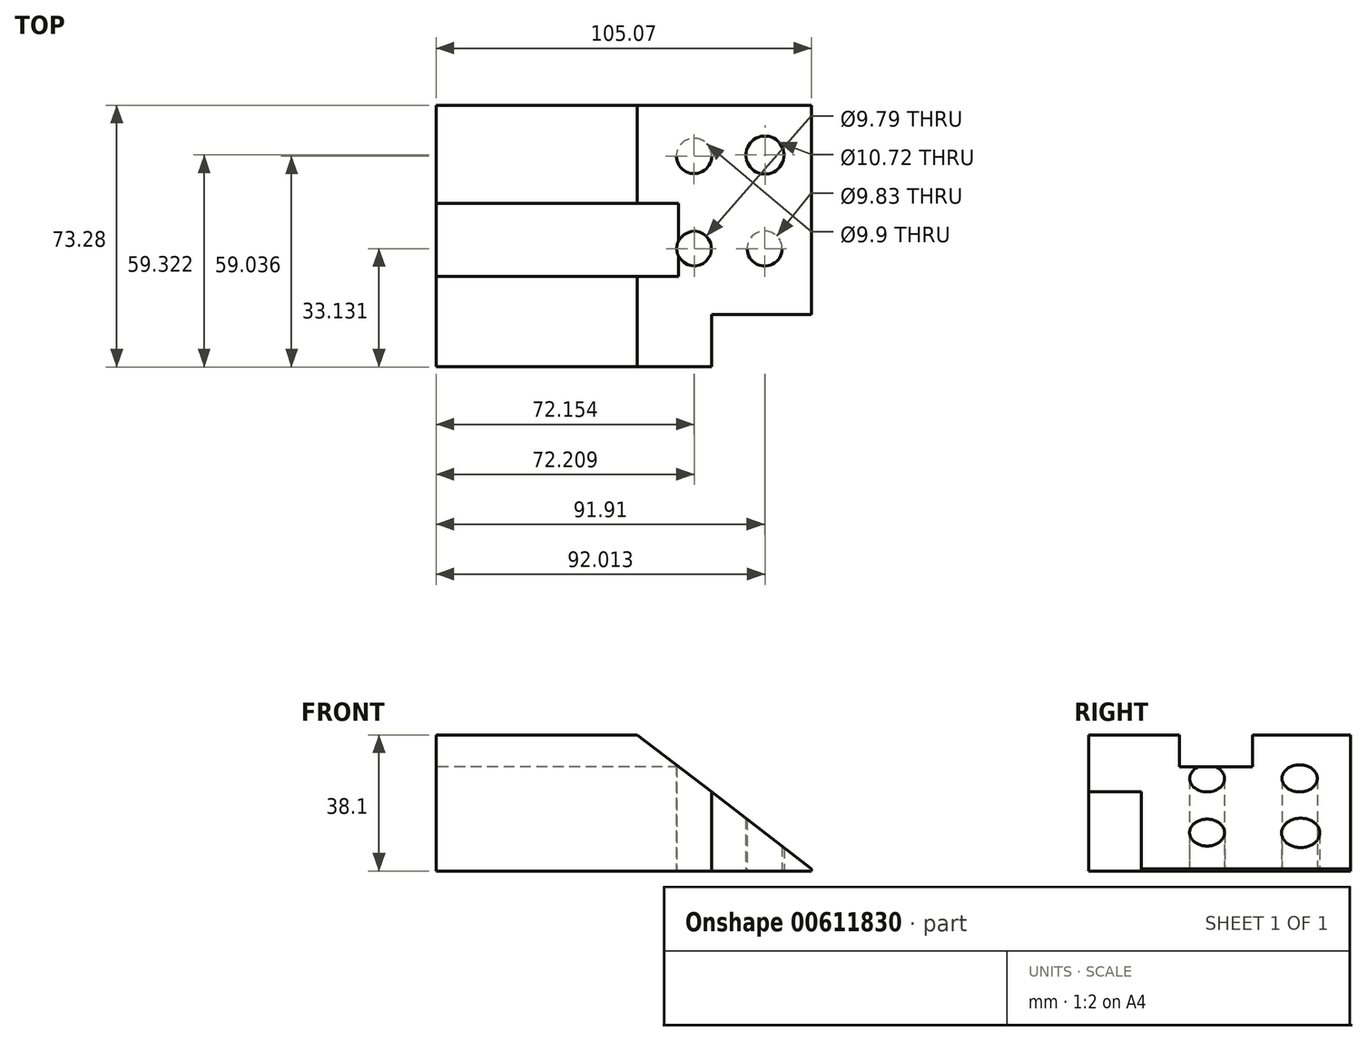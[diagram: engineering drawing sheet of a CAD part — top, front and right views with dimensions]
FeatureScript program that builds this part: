
annotation { "Feature Type Name" : "Feature", "Feature Type Description" : "" }
export const myFeature = defineFeature(function(context is Context, id is Id, definition is map)
    precondition{}
    {
        {
            var Q0;
            Q0=qCreatedBy(makeId("Top.planeOp"),FACE);
            var sketch = newSketch(context, id + "F0", { "sketchPlane" : qUnion([Q0])});
            skLineSegment(sketch, "E0.bottom", {"start": v(0, 0) * mm, "end": v(-59.7, 0) * mm});
            skLineSegment(sketch, "E0.top", {"start": v(0, -73.28) * mm, "end": v(-59.7, -73.28) * mm});
            skLineSegment(sketch, "E0.left", {"start": v(0, 0) * mm, "end": v(0, -73.28) * mm});
            skLineSegment(sketch, "E0.right", {"start": v(-59.7, 0) * mm, "end": v(-59.7, -73.28) * mm});
            skLineSegment(sketch, "E1.bottom", {"start": v(0, 0) * mm, "end": v(45.38, 0) * mm});
            skLineSegment(sketch, "E1.top", {"start": v(0, -73.28) * mm, "end": v(45.38, -73.28) * mm});
            skLineSegment(sketch, "E1.right", {"start": v(45.38, 0) * mm, "end": v(45.38, -73.28) * mm});
            skSolve(sketch);
        }
        {
            var Q0;
            Q0 = qSketchRegion(id + "F0", true);
            extrude(context, id + "F1", {"entities" : qUnion([Q0]), "depth" : 38.1 * mm, "offsetDistance" : 25.4 * mm});
        }
        {
            var Q0;
            Q0=qCreatedBy(makeId("Front.planeOp"),FACE);
            var sketch = newSketch(context, id + "F2", { "sketchPlane" : qUnion([Q0])});
            skLineSegment(sketch, "E2", {"start": v(46.2, 0) * mm, "end": v(-9.07, 42.45) * mm});
            skLineSegment(sketch, "E3", {"start": v(-9.07, 42.45) * mm, "end": v(48.2, 42.45) * mm});
            skLineSegment(sketch, "E4", {"start": v(48.2, 42.45) * mm, "end": v(48.2, 0) * mm});
            skLineSegment(sketch, "E5", {"start": v(48.2, 0) * mm, "end": v(46.2, 0) * mm});
            skSolve(sketch);
        }
        {
            var Q0;
            Q0=makeQuery(id+"F2.imprint","IMPRINT",FACE,{"disambiguationData":[TD([[makeQuery(id+"F2.imprint","IMPRINT",EDGE,{"derivedFrom":sQuery(id+"F2.wireOp",EDGE,"E2")}),-1.0]])]});
            extrude(context, id + "F3", {"entities" : qUnion([Q0]), "operationType" : NewBodyOperationType.REMOVE, "oppositeDirection" : true, "depth" : -76.2 * mm, "offsetDistance" : 25.4 * mm});
        }
        {
            var Q0;
            Q0=makeQuery(id+"F1.opExtrude","SWEPT_FACE",FACE,{"disambiguationData":[OSD([sQuery(id+"F0.wireOp",EDGE,"E0.right")])]});
            var sketch = newSketch(context, id + "F4", { "sketchPlane" : qUnion([Q0])});
            skLineSegment(sketch, "E6", {"start": v(27.49, 38.1) * mm, "end": v(27.49, 29.21) * mm});
            skLineSegment(sketch, "E7", {"start": v(27.49, 29.21) * mm, "end": v(47.92, 29.21) * mm});
            skLineSegment(sketch, "E8", {"start": v(47.92, 29.21) * mm, "end": v(47.92, 38.1) * mm});
            skLineSegment(sketch, "E9", {"start": v(47.92, 38.1) * mm, "end": v(27.49, 38.1) * mm});
            skSolve(sketch);
        }
        {
            var Q0;
            Q0 = qSketchRegion(id + "F4", true);
            extrude(context, id + "F5", {"entities" : qUnion([Q0]), "operationType" : NewBodyOperationType.REMOVE, "oppositeDirection" : true, "depth" : 76.2 * mm, "offsetDistance" : 25.4 * mm});
        }
        {
            var Q0;
            Q0=makeQuery(id+"F1.opExtrude","CAP_FACE",FACE,{"disambiguationData":[OSD([sQuery(id+"F0.wireOp",EDGE,"E0.bottom"),sQuery(id+"F0.wireOp",EDGE,"E0.top"),sQuery(id+"F0.wireOp",EDGE,"E0.right"),sQuery(id+"F0.wireOp",EDGE,"E1.bottom"),sQuery(id+"F0.wireOp",EDGE,"E1.top"),sQuery(id+"F0.wireOp",EDGE,"E1.right")])],"isStart":true});
            var sketch = newSketch(context, id + "F6", { "sketchPlane" : qUnion([Q0])});
            skLineSegment(sketch, "E10", {"start": v(17.41, 73.28) * mm, "end": v(17.41, 58.57) * mm});
            skLineSegment(sketch, "E11", {"start": v(17.41, 58.57) * mm, "end": v(45.38, 58.57) * mm});
            skLineSegment(sketch, "E12", {"start": v(45.38, 58.57) * mm, "end": v(45.38, 73.28) * mm});
            skLineSegment(sketch, "E13", {"start": v(45.38, 73.28) * mm, "end": v(17.41, 73.28) * mm});
            skSolve(sketch);
        }
        {
            var Q0;
            Q0 = qSketchRegion(id + "F6", true);
            extrude(context, id + "F7", {"entities" : qUnion([Q0]), "operationType" : NewBodyOperationType.REMOVE, "oppositeDirection" : true, "depth" : 25.4 * mm, "offsetDistance" : 25.4 * mm});
        }
        {
            var Q0;
            Q0=makeQuery(id+"F1.opExtrude","CAP_FACE",FACE,{"disambiguationData":[OSD([sQuery(id+"F0.wireOp",EDGE,"E0.bottom"),sQuery(id+"F0.wireOp",EDGE,"E0.top"),sQuery(id+"F0.wireOp",EDGE,"E0.right"),sQuery(id+"F0.wireOp",EDGE,"E1.bottom"),sQuery(id+"F0.wireOp",EDGE,"E1.top"),sQuery(id+"F0.wireOp",EDGE,"E1.right")])],"isStart":true});
            var sketch = newSketch(context, id + "F8", { "sketchPlane" : qUnion([Q0])});
            skCircle(sketch, "E14", {"center": v(12.52, 40.15) * mm, "radius": 4.9 * mm});
            skCircle(sketch, "E15", {"center": v(12.46, 14.24) * mm, "radius": 4.95 * mm});
            skCircle(sketch, "E16", {"center": v(32.22, 40.15) * mm, "radius": 4.91 * mm});
            skCircle(sketch, "E17", {"center": v(32.32, 13.96) * mm, "radius": 5.36 * mm});
            skLineSegment(sketch, "E18.trimOffspring", {"start": v(12.52, 40.15) * mm, "end": v(12.36, 40.15) * mm});
            skPoint(sketch, "E19.orphan", {"position": v(12.52, 0) * mm});
            skSolve(sketch);
        }
        {
            var Q0;
            Q0 = qSketchRegion(id + "F8", true);
            extrude(context, id + "F9", {"entities" : qUnion([Q0]), "operationType" : NewBodyOperationType.REMOVE, "oppositeDirection" : true, "depth" : 76.2 * mm, "offsetDistance" : 25.4 * mm});
        }
    });
